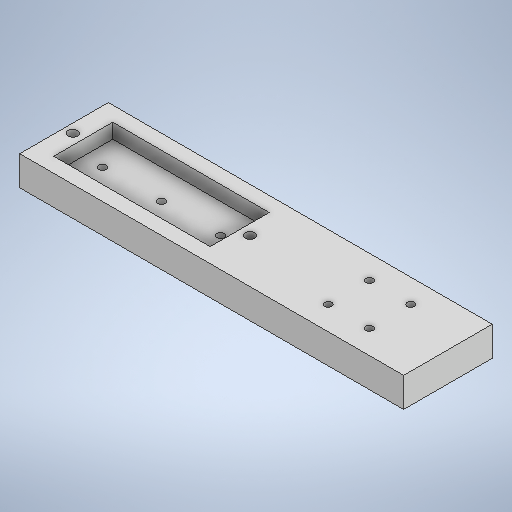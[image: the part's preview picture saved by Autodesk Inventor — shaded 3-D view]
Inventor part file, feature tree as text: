
AUTODESK INVENTOR PART (.ipt)
format: ipt  version: 2025.2 (Build 292293000, 293)  size: 301,568 bytes
history: native  units: mm
features: extrude x6, sketch x6
ambient origin geometry x8: Origin, YZ Plane, XZ Plane, XY Plane, X Axis, Y Axis, Z Axis, Center Point
bodies: Solido1 (feature_tree)
feature tree (12):
  extrude  "Estrusione1"  Depth=30.0mm
  extrude  "Estrusione2"  Depth=130.0mm
  extrude  "Estrusione3"  Depth=10.0mm TaperAngle=0.0deg
  extrude  "Estrusione4"  Depth=20.0mm
  extrude  "Estrusione5"  Depth=5.0mm
  extrude  "Estrusione6"  Depth=70.0mm
  sketch  "Schizzo1"
  sketch  "Schizzo2"
  sketch  "Schizzo3"
  sketch  "Schizzo4"
  sketch  "Schizzo5"
  sketch  "Schizzo6"
